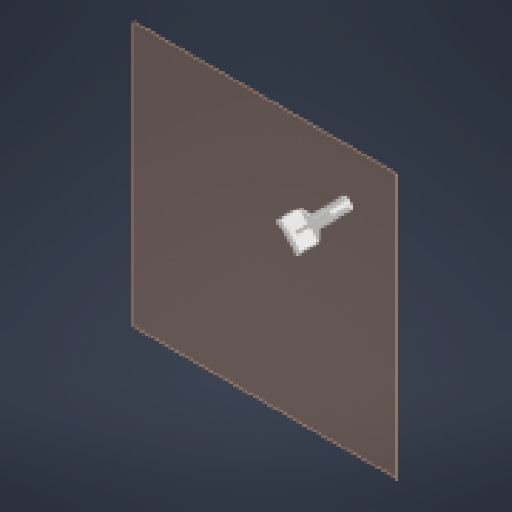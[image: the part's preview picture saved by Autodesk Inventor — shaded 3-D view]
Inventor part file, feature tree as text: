
AUTODESK INVENTOR PART (.ipt)
format: ipt  version: 2023.1 (Build 271208000, 208)  size: 246,272 bytes
history: native  units: mm
features: other x3, extrude x2, chamfer x2, sketch x2, plane x1
ambient origin geometry x8: Origin, YZ Plane, XZ Plane, XY Plane, X Axis, Y Axis, Z Axis, Center Point
bodies: Solid1 (feature_tree)
feature tree (10):
  plane  "Work Plane1"
  extrude  "Extrusion1"  Depth=147.0mm
  extrude  "Extrusion2"  Depth=2.0mm
  chamfer  "Chamfer1"  Distance=7.5mm
  chamfer  "Chamfer2"  Distance=142.0mm
  sketch  "Sketch1"  dims[d0=157.0mm d1=147.0mm]
  sketch  "Sketch2"  dims[d2=45.0deg d3=7.5mm d4=7.5mm d5=142.0mm d6=135.0deg d7=135.0deg d8=22.5mm d9=22.5mm d10=5.0mm d11=2.0mm d12=0.0mm d13=157.0mm d14=7.5mm d16=135.0deg d21=2.0mm d22=2.0mm d23=22.0mm d24=0.0mm d25=60.0mm d26=2.0mm d27=4.0mm d28=45.0deg d29=2.0mm d30=2.0mm d31=45.0deg d32=10.0mm d33=10.0mm d34=10.0mm d35=10.0mm d36=5.0mm d37=2.0mm d38=45.0deg]
  parser-record x1  (decoder bookkeeping rows leaked as tree rows — omitted from the tree; the rows remain in map.json)
  other  "Beau4tClock.iam"
  other  "Clock:1"
note: 1 file-system path scrubbed to <path> (originals preserved in map.json)
